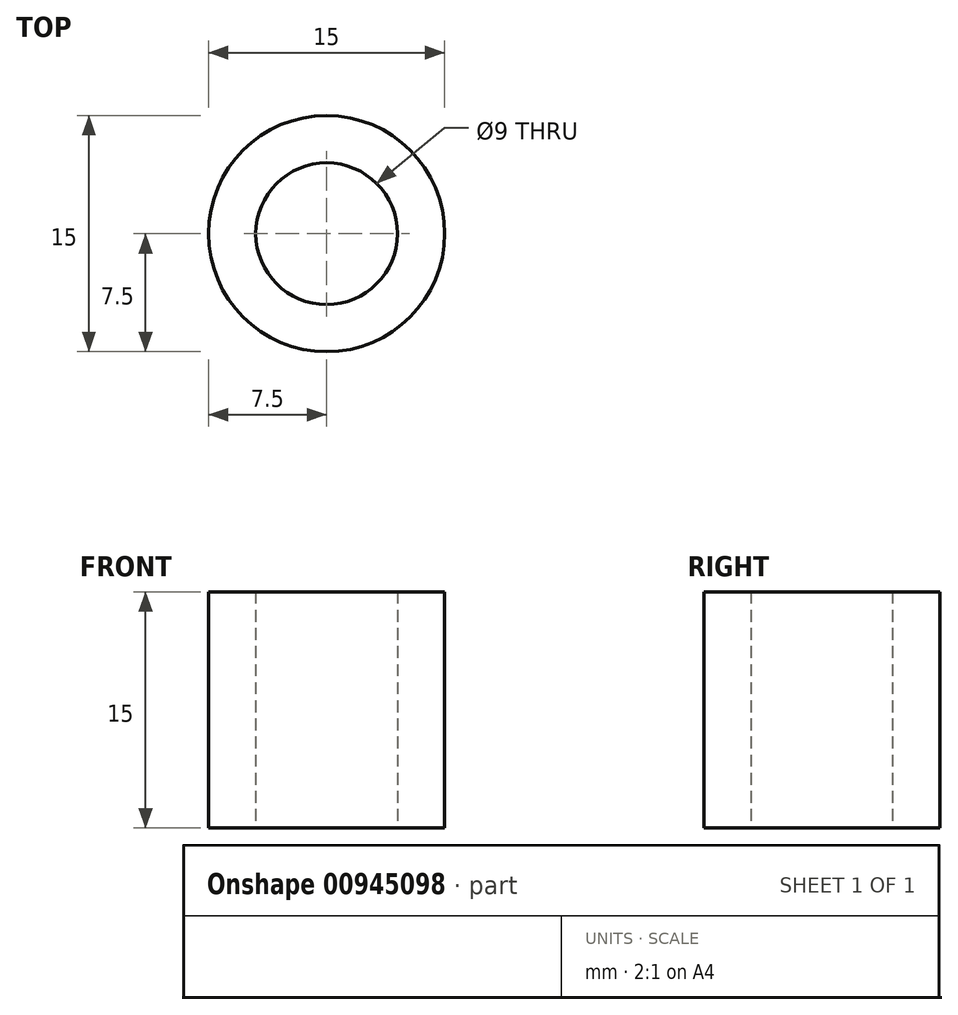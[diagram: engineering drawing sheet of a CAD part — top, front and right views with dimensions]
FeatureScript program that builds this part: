
annotation { "Feature Type Name" : "Feature", "Feature Type Description" : "" }
export const myFeature = defineFeature(function(context is Context, id is Id, definition is map)
    precondition{}
    {
        {
            var Q0;
            Q0=qCreatedBy(makeId("Top.planeOp"),FACE);
            var sketch = newSketch(context, id + "F0", { "sketchPlane" : qUnion([Q0])});
            skCircle(sketch, "E0", {"center": v(0, 0) * mm, "radius": 7.5 * mm});
            skCircle(sketch, "E1", {"center": v(0, 0) * mm, "radius": 4.5 * mm});
            skSolve(sketch);
        }
        {
            var Q0;
            Q0=makeQuery(id+"F0.imprint","IMPRINT",FACE,{"disambiguationData":[TD([[makeQuery(id+"F0.imprint","IMPRINT",EDGE,{"derivedFrom":sQuery(id+"F0.wireOp",EDGE,"E0")}),1.0]])]});
            extrude(context, id + "F1", {"entities" : qUnion([Q0]), "depth" : 15 * mm, "offsetDistance" : 25 * mm});
        }
    });
